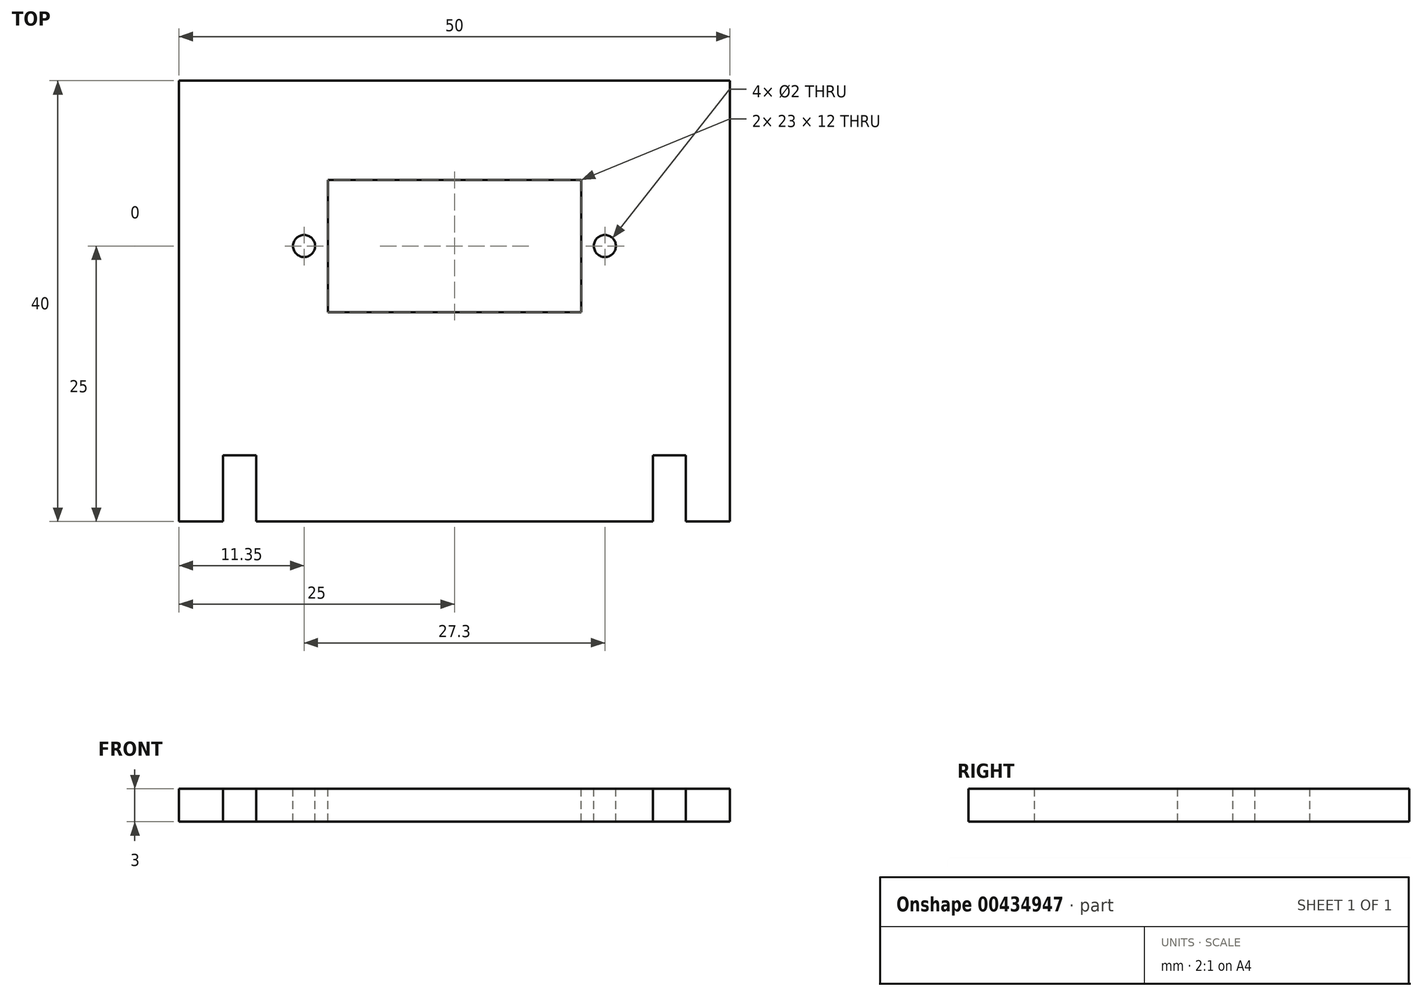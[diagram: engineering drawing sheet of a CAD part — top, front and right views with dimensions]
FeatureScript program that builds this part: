
annotation { "Feature Type Name" : "Feature", "Feature Type Description" : "" }
export const myFeature = defineFeature(function(context is Context, id is Id, definition is map)
    precondition{}
    {
        {
            var Q0;
            Q0=qCreatedBy(makeId("Top.planeOp"),FACE);
            var sketch = newSketch(context, id + "F0", { "sketchPlane" : qUnion([Q0])});
            skLineSegment(sketch, "E0.bottom", {"start": v(25, -25) * mm, "end": v(-25, -25) * mm});
            skLineSegment(sketch, "E0.top", {"start": v(25, 15) * mm, "end": v(-25, 15) * mm});
            skLineSegment(sketch, "E0.left", {"start": v(25, -25) * mm, "end": v(25, 15) * mm});
            skLineSegment(sketch, "E0.right", {"start": v(-25, -25) * mm, "end": v(-25, 15) * mm});
            skPoint(sketch, "E0.middle", {"position": v(0, 0) * mm});
            skSolve(sketch);
        }
        {
            var Q0;
            Q0=makeQuery(id+"F0.imprint","IMPRINT",FACE,{"disambiguationData":[TD([[makeQuery(id+"F0.imprint","IMPRINT",EDGE,{"derivedFrom":sQuery(id+"F0.wireOp",EDGE,"E0.bottom")}),-1.0]])]});
            extrude(context, id + "F1", {"entities" : qUnion([Q0]), "endBound" : BoundingType.SYMMETRIC, "depth" : 3 * mm});
        }
        {
            var Q0;
            Q0=makeQuery(id+"F1.opExtrude","CAP_FACE",FACE,{"disambiguationData":[OSD([sQuery(id+"F0.wireOp",EDGE,"E0.bottom"),sQuery(id+"F0.wireOp",EDGE,"E0.top"),sQuery(id+"F0.wireOp",EDGE,"E0.left"),sQuery(id+"F0.wireOp",EDGE,"E0.right")])],"isStart":false});
            var sketch = newSketch(context, id + "F2", { "sketchPlane" : qUnion([Q0])});
            skLineSegment(sketch, "E1.bottom", {"start": v(11.5, -6) * mm, "end": v(-11.5, -6) * mm});
            skLineSegment(sketch, "E1.top", {"start": v(11.5, 6) * mm, "end": v(-11.5, 6) * mm});
            skLineSegment(sketch, "E1.left", {"start": v(11.5, -6) * mm, "end": v(11.5, 6) * mm});
            skLineSegment(sketch, "E1.right", {"start": v(-11.5, -6) * mm, "end": v(-11.5, 6) * mm});
            skPoint(sketch, "E1.middle", {"position": v(0, 0) * mm});
            skCircle(sketch, "E2", {"center": v(13.65, 0) * mm, "radius": 1 * mm});
            skCircle(sketch, "E3", {"center": v(-13.65, 0) * mm, "radius": 1 * mm});
            skSolve(sketch);
        }
        {
            var Q0;
            Q0=makeQuery(id+"F2.imprint","IMPRINT",FACE,{"disambiguationData":[TD([[makeQuery(id+"F2.imprint","IMPRINT",EDGE,{"derivedFrom":sQuery(id+"F2.wireOp",EDGE,"E1.bottom")}),-1.0]])]});
            var Q1;
            Q1=makeQuery(id+"F2.imprint","IMPRINT",FACE,{"disambiguationData":[TD([[makeQuery(id+"F2.imprint","IMPRINT",EDGE,{"derivedFrom":sQuery(id+"F2.wireOp",EDGE,"E2")}),1.0]])]});
            var Q2;
            Q2=makeQuery(id+"F2.imprint","IMPRINT",FACE,{"disambiguationData":[TD([[makeQuery(id+"F2.imprint","IMPRINT",EDGE,{"derivedFrom":sQuery(id+"F2.wireOp",EDGE,"E3")}),1.0]])]});
            extrude(context, id + "F3", {"entities" : qUnion([Q0, Q1, Q2]), "operationType" : NewBodyOperationType.REMOVE, "oppositeDirection" : true, "depth" : 25 * mm});
        }
        {
            var Q0;
            Q0=makeQuery(id+"F1.opExtrude","CAP_FACE",FACE,{"disambiguationData":[OSD([sQuery(id+"F0.wireOp",EDGE,"E0.bottom"),sQuery(id+"F0.wireOp",EDGE,"E0.top"),sQuery(id+"F0.wireOp",EDGE,"E0.left"),sQuery(id+"F0.wireOp",EDGE,"E0.right")])],"isStart":false});
            var sketch = newSketch(context, id + "F4", { "sketchPlane" : qUnion([Q0])});
            skLineSegment(sketch, "E4.bottom", {"start": v(-21, -25) * mm, "end": v(-18, -25) * mm});
            skLineSegment(sketch, "E4.top", {"start": v(-21, -19) * mm, "end": v(-18, -19) * mm});
            skLineSegment(sketch, "E4.left", {"start": v(-21, -25) * mm, "end": v(-21, -19) * mm});
            skLineSegment(sketch, "E4.right", {"start": v(-18, -25) * mm, "end": v(-18, -19) * mm});
            skLineSegment(sketch, "E5.MirrorCS", {"start": v(18, -25) * mm, "end": v(18, -19) * mm});
            skLineSegment(sketch, "E6.MirrorCS", {"start": v(21, -19) * mm, "end": v(18, -19) * mm});
            skLineSegment(sketch, "E7.MirrorCS", {"start": v(21, -25) * mm, "end": v(18, -25) * mm});
            skLineSegment(sketch, "E8.MirrorCS", {"start": v(21, -25) * mm, "end": v(21, -19) * mm});
            skSolve(sketch);
        }
        {
            var Q0;
            Q0=makeQuery(id+"F4.imprint","IMPRINT",FACE,{"disambiguationData":[TD([[makeQuery(id+"F4.imprint","IMPRINT",EDGE,{"derivedFrom":sQuery(id+"F4.wireOp",EDGE,"E4.bottom")}),-1.0]])]});
            var Q1;
            Q1=makeQuery(id+"F4.imprint","IMPRINT",FACE,{"disambiguationData":[TD([[makeQuery(id+"F4.imprint","IMPRINT",EDGE,{"derivedFrom":sQuery(id+"F4.wireOp",EDGE,"E5.MirrorCS")}),-1.0]])]});
            extrude(context, id + "F5", {"entities" : qUnion([Q0, Q1]), "operationType" : NewBodyOperationType.REMOVE, "oppositeDirection" : true, "depth" : 25 * mm});
        }
    });
